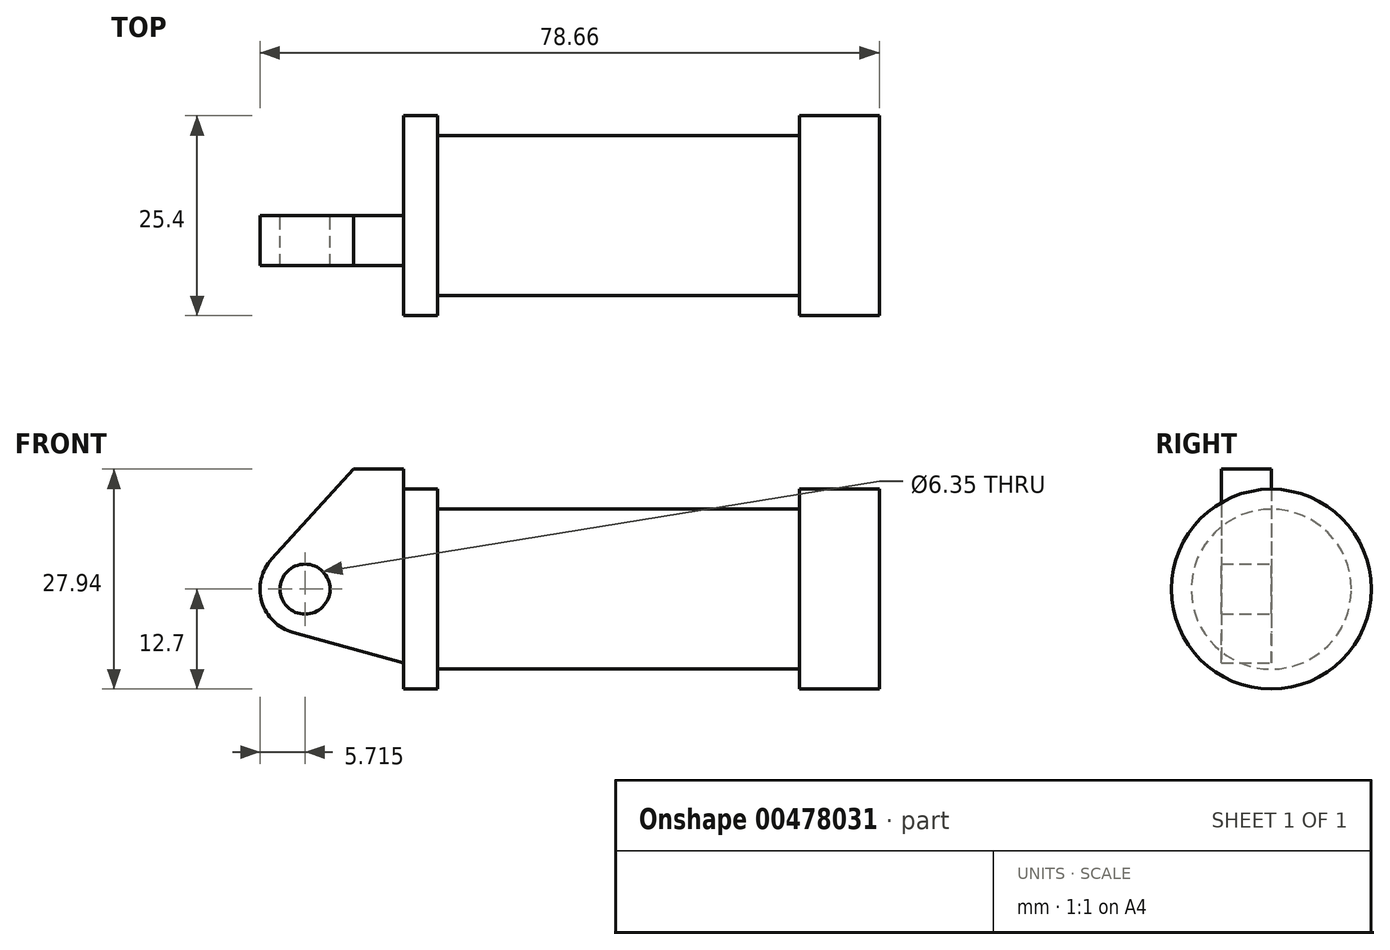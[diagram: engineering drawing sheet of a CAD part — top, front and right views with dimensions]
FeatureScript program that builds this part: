
annotation { "Feature Type Name" : "Feature", "Feature Type Description" : "" }
export const myFeature = defineFeature(function(context is Context, id is Id, definition is map)
    precondition{}
    {
        {
            var Q0;
            Q0=qCreatedBy(makeId("Front.planeOp"),FACE);
            var sketch = newSketch(context, id + "F0", { "sketchPlane" : qUnion([Q0])});
            skLineSegment(sketch, "E0", {"start": v(0, 0) * mm, "end": v(0, 12.7) * mm});
            skLineSegment(sketch, "E1", {"start": v(0, 12.7) * mm, "end": v(10.16, 12.7) * mm});
            skLineSegment(sketch, "E2", {"start": v(10.16, 12.7) * mm, "end": v(10.16, 10.16) * mm});
            skLineSegment(sketch, "E3", {"start": v(10.16, 10.16) * mm, "end": v(56.13, 10.16) * mm});
            skLineSegment(sketch, "E4", {"start": v(56.13, 10.16) * mm, "end": v(56.13, 12.7) * mm});
            skLineSegment(sketch, "E5", {"start": v(56.13, 12.7) * mm, "end": v(66.3, 12.7) * mm});
            skLineSegment(sketch, "E6", {"start": v(66.3, 12.7) * mm, "end": v(66.3, 0) * mm});
            skLineSegment(sketch, "E7", {"start": v(66.3, 0) * mm, "end": v(0, 0) * mm});
            skLineSegment(sketch, "E8", {"start": v(5.84, 15.24) * mm, "end": v(-0.5, 15.24) * mm});
            skLineSegment(sketch, "E9", {"start": v(-0.5, 15.24) * mm, "end": v(-10.88, 3.85) * mm});
            skLineSegment(sketch, "E10", {"start": v(0, 0) * mm, "end": v(-6.65, 0) * mm});
            skCircle(sketch, "E11", {"center": v(-6.65, 0) * mm, "radius": 5.72 * mm});
            skCircle(sketch, "E12", {"center": v(-6.65, 0) * mm, "radius": 3.18 * mm});
            skLineSegment(sketch, "E13", {"start": v(5.84, 15.24) * mm, "end": v(5.84, -9.4) * mm});
            skLineSegment(sketch, "E14", {"start": v(5.84, -9.4) * mm, "end": v(-8.18, -5.5) * mm});
            skSolve(sketch);
        }
        {
            var Q0;
            {var subQ0=sQuery(id+"F0.wireOp",EDGE,"E2");Q0=makeQuery(id+"F0.imprint","IMPRINT",FACE,{"disambiguationData":[TD([[makeQuery(id+"F0.imprint","IMPRINT",EDGE,{"derivedFrom":subQ0}),-1.0]])]});}
            var Q1;
            Q1=sQuery(id+"F0.wireOp",EDGE,"E7");
            revolve(context, id + "F1", {"entities" : qUnion([Q0]), "axis" : qUnion([Q1]), "revolveType" : RevolveType.FULL});
        }
        {
            var Q0;
            {var subQ1=sQuery(id+"F0.wireOp",EDGE,"E0");Q0=makeQuery(id+"F0.imprint","IMPRINT",FACE,{"disambiguationData":[TD([[makeQuery(id+"F0.imprint","IMPRINT",EDGE,{"derivedFrom":subQ1}),1.0]])]});}
            var Q1;
            {var subQ0=sQuery(id+"F0.wireOp",EDGE,"E0");Q1=makeQuery(id+"F0.imprint","IMPRINT",FACE,{"disambiguationData":[TD([[makeQuery(id+"F0.imprint","IMPRINT",EDGE,{"derivedFrom":subQ0}),-1.0]])]});}
            var Q2;
            {var subQ0=sQuery(id+"F0.wireOp",EDGE,"E14");Q2=makeQuery(id+"F0.imprint","IMPRINT",FACE,{"disambiguationData":[TD([[makeQuery(id+"F0.imprint","IMPRINT",EDGE,{"derivedFrom":subQ0}),-1.0]])]});}
            var Q3;
            {var subQ5=sQuery(id+"F0.wireOp",EDGE,"E12");Q3=makeQuery(id+"F0.imprint","IMPRINT",FACE,{"disambiguationData":[TD([[makeQuery(id+"F0.imprint","IMPRINT",EDGE,{"derivedFrom":subQ5}),-1.0]])]});}
            extrude(context, id + "F2", {"entities" : qUnion([Q0, Q1, Q2, Q3]), "operationType" : NewBodyOperationType.ADD, "depth" : 6.35 * mm});
        }
    });
